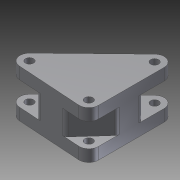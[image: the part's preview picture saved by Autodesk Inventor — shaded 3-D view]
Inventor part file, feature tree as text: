
AUTODESK INVENTOR PART (.ipt)
format: ipt  version: 2011 SP2 (Build 150309200, 309)  size: 154,112 bytes
history: native  units: mm
features: sketch x3, extrude x2, hole x1, fillet x1
ambient origin geometry x8: Origin, YZ Plane, XZ Plane, XY Plane, X Axis, Y Axis, Z Axis, Center Point
bodies: Solid1 (feature_tree)
feature tree (7):
  extrude  "Extrusion1"  Depth=33.421041mm
  extrude  "Extrusion2"  Depth=5.21368mm
  hole  "Hole1"  [1 undecoded]
  fillet  "Fillet1"  Radius=26.80368mm
  sketch  "Sketch1"  dims[d0=25.4mm d1=33.421041mm]
  sketch  "Sketch2"  dims[d2=10.02632mm d3=5.21368mm]
  sketch  "Sketch3"  dims[d4=27.739467mm d5=26.268959mm d7=26.80368mm d8=37.297893mm d9=26.335787mm d10=24.531041mm d11=43.915254mm d12=32.752538mm d13=38.1mm d6=37.297893mm d14=27.739467mm d15=26.80368mm d16=20.0mm d17=0.0mm d18=4.0mm d19=10.0mm d20=0.0mm d21=3.4mm d22=6.0mm d23=4.4mm d24=3.0mm d25=90.0deg d26=8.0mm d27=20.594885mm d28=2.0mm]
note: 1 required parameter value undecoded (feature->parameter linkage not recoverable at this tier; creation-order binding heuristic only, values carry confidence <= 0.55)
